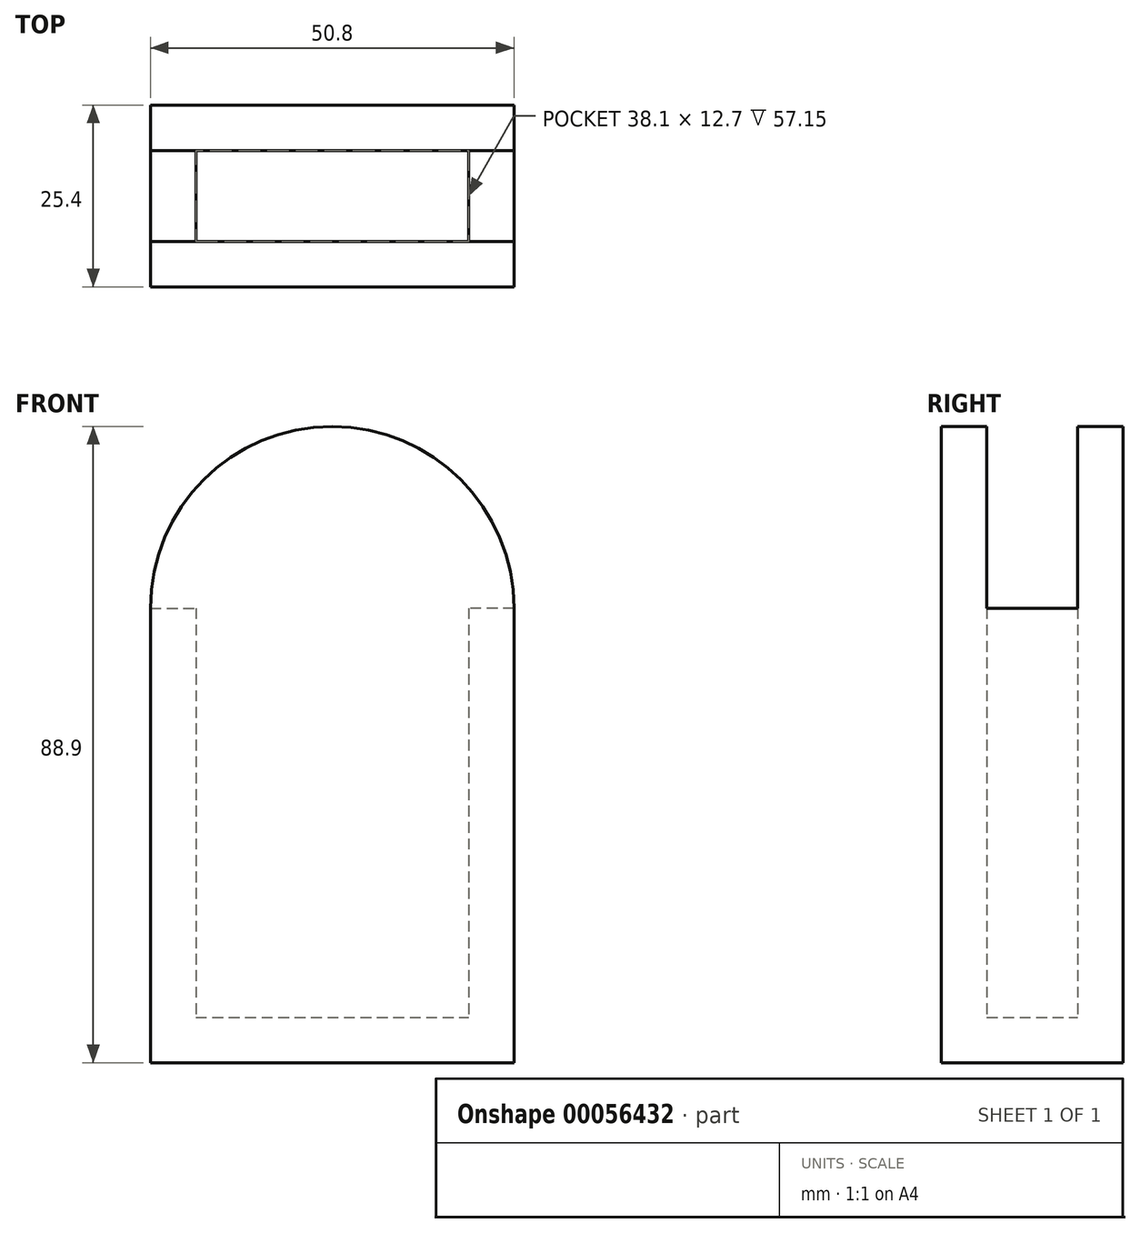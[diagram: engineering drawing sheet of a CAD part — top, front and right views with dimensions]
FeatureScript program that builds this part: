
annotation { "Feature Type Name" : "Feature", "Feature Type Description" : "" }
export const myFeature = defineFeature(function(context is Context, id is Id, definition is map)
    precondition{}
    {
        {
            var Q0;
            Q0=qCreatedBy(makeId("Front.planeOp"),FACE);
            var sketch = newSketch(context, id + "F0", { "sketchPlane" : qUnion([Q0])});
            skCircle(sketch, "E0", {"center": v(0, 0) * mm, "radius": 25.4 * mm});
            skLineSegment(sketch, "E1.bottom", {"start": v(-25.4, 0) * mm, "end": v(25.4, 0) * mm});
            skLineSegment(sketch, "E1.top", {"start": v(-25.4, -63.5) * mm, "end": v(25.4, -63.5) * mm});
            skLineSegment(sketch, "E1.left", {"start": v(-25.4, 0) * mm, "end": v(-25.4, -63.5) * mm});
            skLineSegment(sketch, "E1.right", {"start": v(25.4, 0) * mm, "end": v(25.4, -63.5) * mm});
            skLineSegment(sketch, "E2", {"start": v(-25.4, -25.4) * mm, "end": v(25.4, -25.4) * mm});
            skCircle(sketch, "E3", {"center": v(0, -50.8) * mm, "radius": 25.4 * mm});
            skSolve(sketch);
        }
        {
            var Q0;
            {var subQ0=sQuery(id+"F0.wireOp",EDGE,"E1.bottom");Q0=makeQuery(id+"F0.imprint","IMPRINT",FACE,{"disambiguationData":[TD([[makeQuery(id+"F0.imprint","IMPRINT",EDGE,{"derivedFrom":subQ0}),1.0]])]});}
            var Q1;
            {var subQ0=sQuery(id+"F0.wireOp",EDGE,"E1.bottom");Q1=makeQuery(id+"F0.imprint","IMPRINT",FACE,{"disambiguationData":[TD([[makeQuery(id+"F0.imprint","IMPRINT",EDGE,{"derivedFrom":subQ0}),-1.0]])]});}
            var Q2;
            {var subQ0=sQuery(id+"F0.wireOp",EDGE,"E1.left");var subQ3=sQuery(id+"F0.wireOp",EDGE,"E2");var subQ5=makeQuery(id+"F0.imprint","INTERSECT",VERTEX,{"derivedFrom":[subQ0,subQ3]});Q2=makeQuery(id+"F0.imprint","IMPRINT",FACE,{"disambiguationData":[TD([[makeQuery(id+"F0.imprint","IMPRINT",EDGE,{"disambiguationData":[TD([[subQ5,1.0]])],"derivedFrom":subQ0}),1.0]])]});}
            var Q3;
            {var subQ0=sQuery(id+"F0.wireOp",EDGE,"E1.right");var subQ3=sQuery(id+"F0.wireOp",EDGE,"E2");var subQ5=makeQuery(id+"F0.imprint","INTERSECT",VERTEX,{"derivedFrom":[subQ0,subQ3]});Q3=makeQuery(id+"F0.imprint","IMPRINT",FACE,{"disambiguationData":[TD([[makeQuery(id+"F0.imprint","IMPRINT",EDGE,{"disambiguationData":[TD([[subQ5,1.0]])],"derivedFrom":subQ0}),-1.0]])]});}
            var Q4;
            {var subQ0=sQuery(id+"F0.wireOp",EDGE,"E2");var subQ1=sQuery(id+"F0.wireOp",EDGE,"E1.left");var subQ2=makeQuery(id+"F0.imprint","INTERSECT",VERTEX,{"derivedFrom":[subQ1,subQ0]});Q4=makeQuery(id+"F0.imprint","IMPRINT",FACE,{"disambiguationData":[TD([[makeQuery(id+"F0.imprint","IMPRINT",EDGE,{"disambiguationData":[TD([[subQ2,-1.0]])],"derivedFrom":subQ1}),1.0]])]});}
            var Q5;
            {var subQ0=sQuery(id+"F0.wireOp",EDGE,"E2");var subQ1=sQuery(id+"F0.wireOp",EDGE,"E1.right");var subQ2=makeQuery(id+"F0.imprint","INTERSECT",VERTEX,{"derivedFrom":[subQ1,subQ0]});Q5=makeQuery(id+"F0.imprint","IMPRINT",FACE,{"disambiguationData":[TD([[makeQuery(id+"F0.imprint","IMPRINT",EDGE,{"disambiguationData":[TD([[subQ2,-1.0]])],"derivedFrom":subQ1}),-1.0]])]});}
            var Q6;
            {var subQ0=sQuery(id+"F0.wireOp",EDGE,"E1.left");var subQ1=sQuery(id+"F0.wireOp",EDGE,"E1.top");var subQ2=makeQuery(id+"F0.imprint","INTERSECT",VERTEX,{"derivedFrom":[subQ1,subQ0]});Q6=makeQuery(id+"F0.imprint","IMPRINT",FACE,{"disambiguationData":[TD([[makeQuery(id+"F0.imprint","IMPRINT",EDGE,{"disambiguationData":[TD([[subQ2,-1.0]])],"derivedFrom":subQ1}),1.0]])]});}
            var Q7;
            {var subQ0=sQuery(id+"F0.wireOp",EDGE,"E3");var subQ1=sQuery(id+"F0.wireOp",EDGE,"E1.top");var subQ2=makeQuery(id+"F0.imprint","INTERSECT",VERTEX,{"disambiguationData":[OD(0.0)],"derivedFrom":[subQ1,subQ0]});Q7=makeQuery(id+"F0.imprint","IMPRINT",FACE,{"disambiguationData":[TD([[makeQuery(id+"F0.imprint","IMPRINT",EDGE,{"disambiguationData":[TD([[subQ2,-1.0]])],"derivedFrom":subQ1}),1.0]])]});}
            var Q8;
            {var subQ0=sQuery(id+"F0.wireOp",EDGE,"E1.right");var subQ1=sQuery(id+"F0.wireOp",EDGE,"E1.top");var subQ2=makeQuery(id+"F0.imprint","INTERSECT",VERTEX,{"derivedFrom":[subQ1,subQ0]});Q8=makeQuery(id+"F0.imprint","IMPRINT",FACE,{"disambiguationData":[TD([[makeQuery(id+"F0.imprint","IMPRINT",EDGE,{"disambiguationData":[TD([[subQ2,1.0]])],"derivedFrom":subQ1}),1.0]])]});}
            extrude(context, id + "F1", {"entities" : qUnion([Q0, Q1, Q2, Q3, Q4, Q5, Q6, Q7, Q8]), "endBound" : BoundingType.SYMMETRIC, "depth" : 25.4 * mm});
        }
        {
            var Q0;
            Q0=makeQuery(id+"F1.opExtrude","SWEPT_FACE",FACE,{"disambiguationData":[OSD([sQuery(id+"F0.wireOp",EDGE,"E0")])]});
            shell(context, id + "F2", {"entities" : qUnion([Q0]), "thickness" : 6.35 * mm});
        }
    });
